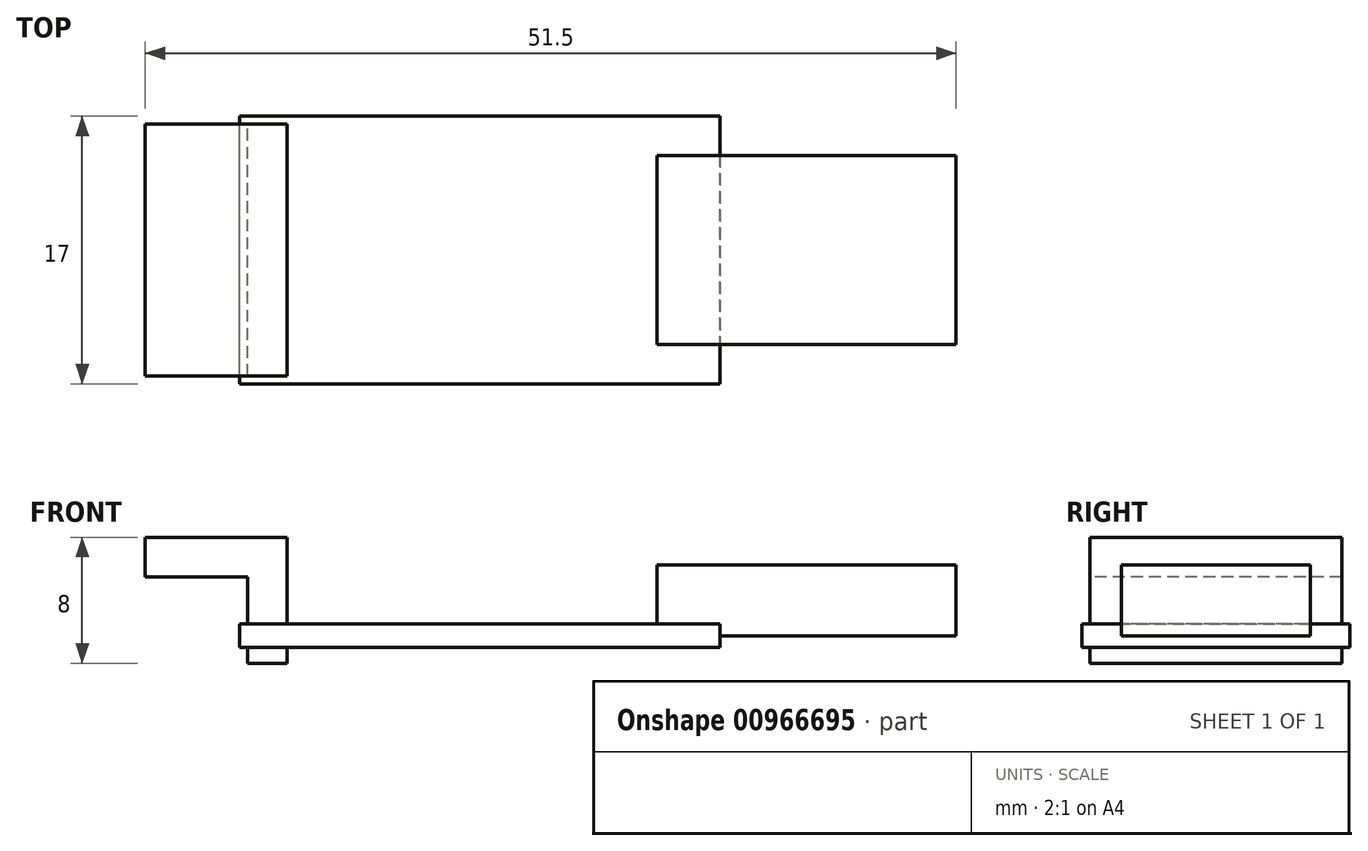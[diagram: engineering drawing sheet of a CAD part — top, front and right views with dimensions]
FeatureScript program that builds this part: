
annotation { "Feature Type Name" : "Feature", "Feature Type Description" : "" }
export const myFeature = defineFeature(function(context is Context, id is Id, definition is map)
    precondition{}
    {
        {
            var Q0;
            Q0=qCreatedBy(makeId("Top.planeOp"),FACE);
            var sketch = newSketch(context, id + "F0", { "sketchPlane" : qUnion([Q0])});
            skLineSegment(sketch, "E0.bottom", {"start": v(15.25, -8.5) * mm, "end": v(-15.25, -8.5) * mm});
            skLineSegment(sketch, "E0.top", {"start": v(15.25, 8.5) * mm, "end": v(-15.25, 8.5) * mm});
            skLineSegment(sketch, "E0.left", {"start": v(15.25, -8.5) * mm, "end": v(15.25, 8.5) * mm});
            skLineSegment(sketch, "E0.right", {"start": v(-15.25, -8.5) * mm, "end": v(-15.25, 8.5) * mm});
            skPoint(sketch, "E0.middle", {"position": v(0, 0) * mm});
            skSolve(sketch);
        }
        {
            var Q0;
            Q0 = qSketchRegion(id + "F0", true);
            extrude(context, id + "F1", {"entities" : qUnion([Q0]), "depth" : 1.5 * mm, "offsetDistance" : 25 * mm});
        }
        {
            var Q0;
            Q0=makeQuery(id+"F1.opExtrude","SWEPT_FACE",FACE,{"disambiguationData":[OSD([sQuery(id+"F0.wireOp",EDGE,"E0.bottom")])]});
            cPlane(context, id + "F2", {"entities" : qUnion([Q0]), "cplaneType" : CPlaneType.OFFSET, "offset" : 2.5 * mm, "oppositeDirection" : true, "width" : 150 * mm, "height" : 150 * mm});
        }
        {
            var Q0;
            Q0=qCreatedBy(id+"F2.planeOp",FACE);
            var sketch = newSketch(context, id + "F3", { "sketchPlane" : qUnion([Q0])});
            skLineSegment(sketch, "E1", {"start": v(15.25, 1.5) * mm, "end": v(15.25, 0.75) * mm});
            skLineSegment(sketch, "E2", {"start": v(15.25, 0.75) * mm, "end": v(30.25, 0.75) * mm});
            skLineSegment(sketch, "E3", {"start": v(30.25, 0.75) * mm, "end": v(30.25, 5.25) * mm});
            skLineSegment(sketch, "E4", {"start": v(30.25, 5.25) * mm, "end": v(11.25, 5.25) * mm});
            skLineSegment(sketch, "E5", {"start": v(11.25, 5.25) * mm, "end": v(11.25, 1.5) * mm});
            skLineSegment(sketch, "E6", {"start": v(11.25, 1.5) * mm, "end": v(15.25, 1.5) * mm});
            skSolve(sketch);
        }
        {
            var Q0;
            Q0 = qSketchRegion(id + "F3", true);
            extrude(context, id + "F4", {"entities" : qUnion([Q0]), "oppositeDirection" : true, "depth" : 12 * mm, "offsetDistance" : 25 * mm});
        }
        {
            var Q0;
            Q0=makeQuery(id+"F1.opExtrude","SWEPT_FACE",FACE,{"disambiguationData":[OSD([sQuery(id+"F0.wireOp",EDGE,"E0.bottom")])]});
            cPlane(context, id + "F5", {"entities" : qUnion([Q0]), "cplaneType" : CPlaneType.OFFSET, "offset" : 0.5 * mm, "oppositeDirection" : true, "width" : 150 * mm, "height" : 150 * mm});
        }
        {
            var Q0;
            Q0=qCreatedBy(id+"F5.planeOp",FACE);
            var sketch = newSketch(context, id + "F6", { "sketchPlane" : qUnion([Q0])});
            skLineSegment(sketch, "E7", {"start": v(-15.25, 1.5) * mm, "end": v(-14.75, 1.5) * mm, "construction": true});
            skLineSegment(sketch, "E8", {"start": v(-14.75, 1.5) * mm, "end": v(-12.25, 1.5) * mm});
            skLineSegment(sketch, "E9", {"start": v(-14.75, 1.5) * mm, "end": v(-14.75, 4.5) * mm});
            skLineSegment(sketch, "E10", {"start": v(-12.25, 1.5) * mm, "end": v(-12.25, 4.5) * mm});
            skLineSegment(sketch, "E11", {"start": v(-14.75, 4.5) * mm, "end": v(-14.75, 7) * mm});
            skLineSegment(sketch, "E12", {"start": v(-12.25, 4.5) * mm, "end": v(-12.25, 7) * mm});
            skLineSegment(sketch, "E13", {"start": v(-12.25, 7) * mm, "end": v(-21.25, 7) * mm});
            skLineSegment(sketch, "E14", {"start": v(-21.25, 7) * mm, "end": v(-21.25, 4.5) * mm});
            skLineSegment(sketch, "E15", {"start": v(-21.25, 4.5) * mm, "end": v(-12.25, 4.5) * mm});
            skSolve(sketch);
        }
        {
            var Q0;
            Q0 = qSketchRegion(id + "F6", true);
            extrude(context, id + "F7", {"entities" : qUnion([Q0]), "oppositeDirection" : true, "depth" : 16 * mm, "offsetDistance" : 25 * mm});
        }
        {
            var Q0;
            Q0=makeQuery(id+"F1.opExtrude","CAP_FACE",FACE,{"disambiguationData":[OSD([sQuery(id+"F0.wireOp",EDGE,"E0.bottom"),sQuery(id+"F0.wireOp",EDGE,"E0.top"),sQuery(id+"F0.wireOp",EDGE,"E0.left"),sQuery(id+"F0.wireOp",EDGE,"E0.right")])],"isStart":true});
            var sketch = newSketch(context, id + "F8", { "sketchPlane" : qUnion([Q0])});
            skLineSegment(sketch, "E16.bottom", {"start": v(-14.75, 8) * mm, "end": v(-12.25, 8) * mm});
            skLineSegment(sketch, "E16.top", {"start": v(-14.75, -8) * mm, "end": v(-12.25, -8) * mm});
            skLineSegment(sketch, "E16.left", {"start": v(-14.75, 8) * mm, "end": v(-14.75, -8) * mm});
            skLineSegment(sketch, "E16.right", {"start": v(-12.25, 8) * mm, "end": v(-12.25, -8) * mm});
            skSolve(sketch);
        }
        {
            var Q0;
            Q0 = qSketchRegion(id + "F8", true);
            extrude(context, id + "F9", {"entities" : qUnion([Q0]), "depth" : 1 * mm, "offsetDistance" : 25 * mm});
        }
    });
